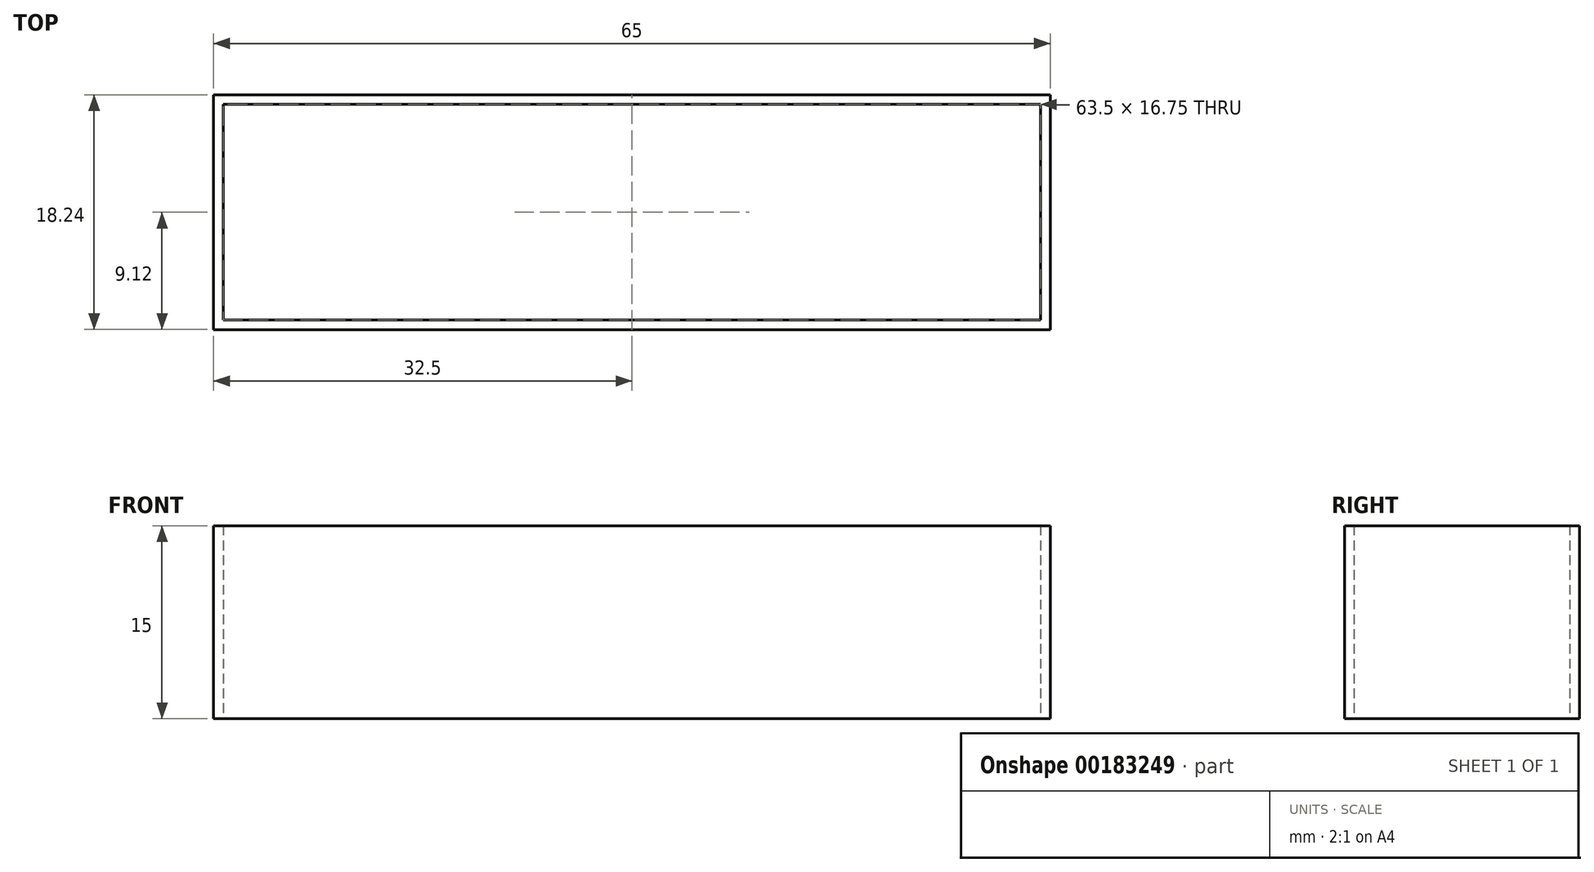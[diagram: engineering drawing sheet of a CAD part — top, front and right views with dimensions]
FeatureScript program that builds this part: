
annotation { "Feature Type Name" : "Feature", "Feature Type Description" : "" }
export const myFeature = defineFeature(function(context is Context, id is Id, definition is map)
    precondition{}
    {
        {
            var Q0;
            Q0=qCreatedBy(makeId("Top.planeOp"),FACE);
            var sketch = newSketch(context, id + "F0", { "sketchPlane" : qUnion([Q0])});
            skLineSegment(sketch, "E0.bottom", {"start": v(32.5, -9.12) * mm, "end": v(-32.5, -9.13) * mm});
            skLineSegment(sketch, "E0.top", {"start": v(32.5, 9.13) * mm, "end": v(-32.5, 9.12) * mm});
            skLineSegment(sketch, "E0.left", {"start": v(32.5, -9.12) * mm, "end": v(32.5, 9.13) * mm});
            skLineSegment(sketch, "E0.right", {"start": v(-32.5, -9.13) * mm, "end": v(-32.5, 9.12) * mm});
            skPoint(sketch, "E0.middle", {"position": v(0, 0) * mm});
            skLineSegment(sketch, "E1.bottom", {"start": v(31.75, -8.37) * mm, "end": v(-31.75, -8.38) * mm});
            skLineSegment(sketch, "E1.top", {"start": v(31.75, 8.38) * mm, "end": v(-31.75, 8.38) * mm});
            skLineSegment(sketch, "E1.left", {"start": v(31.75, -8.37) * mm, "end": v(31.75, 8.38) * mm});
            skLineSegment(sketch, "E1.right", {"start": v(-31.75, -8.38) * mm, "end": v(-31.75, 8.38) * mm});
            skSolve(sketch);
        }
        {
            var Q0;
            Q0=makeQuery(id+"F0.imprint","IMPRINT",FACE,{"disambiguationData":[TD([[makeQuery(id+"F0.imprint","IMPRINT",EDGE,{"derivedFrom":sQuery(id+"F0.wireOp",EDGE,"E0.bottom")}),-1.0]])]});
            extrude(context, id + "F1", {"entities" : qUnion([Q0]), "depth" : 15 * mm});
        }
    });
